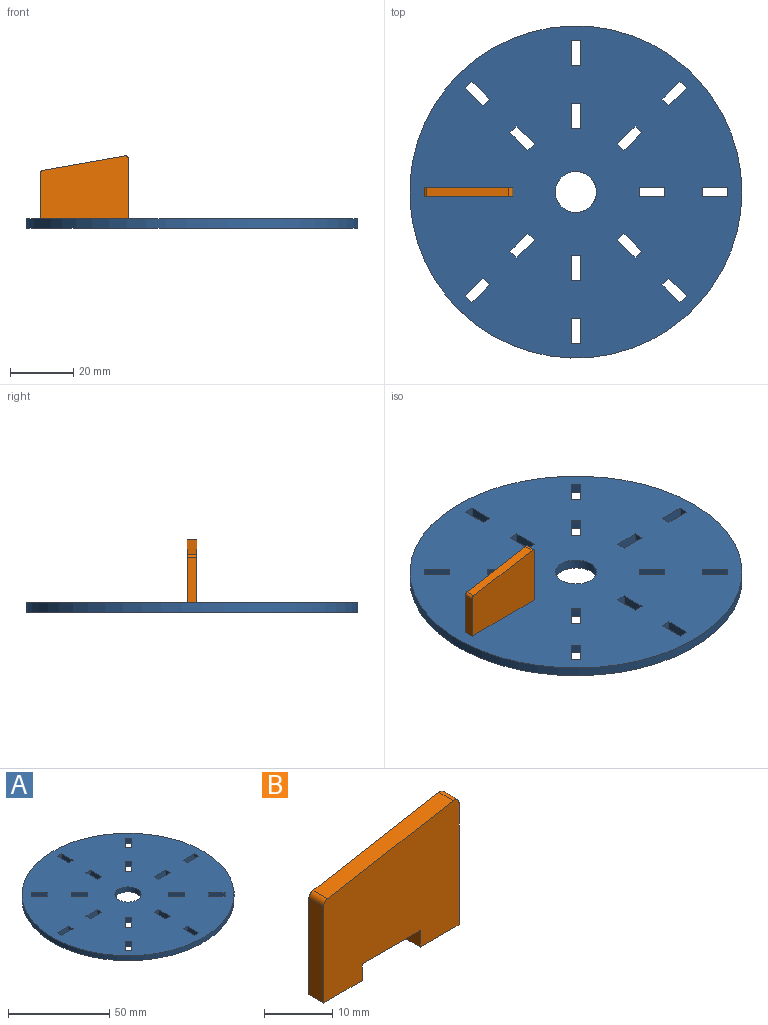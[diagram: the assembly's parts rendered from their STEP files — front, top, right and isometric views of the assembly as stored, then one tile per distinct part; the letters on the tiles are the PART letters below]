
ASSEMBLY  parts=2 mates=1
PART A: 68 faces, bbox 105x105x3 mm
  f0: plane 5.66x5.66mm, normal (-0.71,-0.71,0), area 24mm2, adj f1,f3,f56,f57
  f1: plane 3x2.13mm, normal (0.71,-0.71,0), area 9mm2, adj f0,f2,f56,f57
  f2: plane 5.66x5.66mm, normal (0.71,0.71,0), area 24mm2, adj f1,f3,f56,f57
  f3: plane 3x2.13mm, normal (-0.71,0.71,0), area 9mm2, adj f0,f2,f56,f57
  f4: plane 3x2.13mm, normal (-0.71,0.71,0), area 9mm2, adj f5,f7,f56,f57
  f5: plane 5.66x5.66mm, normal (0.71,0.71,0), area 24mm2, adj f4,f6,f56,f57
  f6: plane 3x2.13mm, normal (0.71,-0.71,0), area 9mm2, adj f5,f7,f56,f57
  f7: plane 5.66x5.66mm, normal (-0.71,-0.71,0), area 24mm2, adj f4,f6,f56,f57
  f8: plane 8.01x3mm, normal (-1,0,0), area 24mm2, adj f9,f11,f56,f57
  f9: plane 3.01x3mm, normal (0,-1,0), area 9mm2, adj f8,f10,f56,f57
  f10: plane 8.01x3mm, normal (1,0,0), area 24mm2, adj f9,f11,f56,f57
  f11: plane 3.01x3mm, normal (0,1,0), area 9mm2, adj f8,f10,f56,f57
  f12: plane 3.01x3mm, normal (0,1,0), area 9mm2, adj f13,f15,f56,f57
  f13: plane 8.01x3mm, normal (1,0,0), area 24mm2, adj f12,f14,f56,f57
  f14: plane 3.01x3mm, normal (0,-1,0), area 9mm2, adj f13,f15,f56,f57
  f15: plane 8.01x3mm, normal (-1,0,0), area 24mm2, adj f12,f14,f56,f57
  f16: plane 5.66x5.66mm, normal (-0.71,0.71,0), area 24mm2, adj f17,f19,f56,f57
  f17: plane 3x2.13mm, normal (-0.71,-0.71,0), area 9mm2, adj f16,f18,f56,f57
  f18: plane 5.66x5.66mm, normal (0.71,-0.71,0), area 24mm2, adj f17,f19,f56,f57
  f19: plane 3x2.13mm, normal (0.71,0.71,0), area 9mm2, adj f16,f18,f56,f57
  f20: plane 3x2.13mm, normal (0.71,0.71,0), area 9mm2, adj f21,f23,f56,f57
  f21: plane 5.66x5.66mm, normal (0.71,-0.71,0), area 24mm2, adj f20,f22,f56,f57
  f22: plane 3x2.13mm, normal (-0.71,-0.71,0), area 9mm2, adj f21,f23,f56,f57
  f23: plane 5.66x5.66mm, normal (-0.71,0.71,0), area 24mm2, adj f20,f22,f56,f57
  f24: plane 8.01x3mm, normal (0,1,0), area 24mm2, adj f25,f27,f56,f57
  f25: plane 3.01x3mm, normal (-1,0,0), area 9mm2, adj f24,f26,f56,f57
  f26: plane 8.01x3mm, normal (0,-1,0), area 24mm2, adj f25,f27,f56,f57
  f27: plane 3.01x3mm, normal (1,0,0), area 9mm2, adj f24,f26,f56,f57
  f28: plane 3.01x3mm, normal (1,0,0), area 9mm2, adj f29,f31,f56,f57
  f29: plane 8.01x3mm, normal (0,-1,0), area 24mm2, adj f28,f30,f56,f57
  f30: plane 3.01x3mm, normal (-1,0,0), area 9mm2, adj f29,f31,f56,f57
  f31: plane 8.01x3mm, normal (0,1,0), area 24mm2, adj f28,f30,f56,f57
  f32: plane 5.66x5.66mm, normal (0.71,0.71,0), area 24mm2, adj f33,f35,f56,f57
  f33: plane 3x2.13mm, normal (-0.71,0.71,0), area 9mm2, adj f32,f34,f56,f57
  f34: plane 5.66x5.66mm, normal (-0.71,-0.71,0), area 24mm2, adj f33,f35,f56,f57
  f35: plane 3x2.13mm, normal (0.71,-0.71,0), area 9mm2, adj f32,f34,f56,f57
  f36: plane 3x2.13mm, normal (0.71,-0.71,0), area 9mm2, adj f37,f39,f56,f57
  f37: plane 5.66x5.66mm, normal (-0.71,-0.71,0), area 24mm2, adj f36,f38,f56,f57
  f38: plane 3x2.13mm, normal (-0.71,0.71,0), area 9mm2, adj f37,f39,f56,f57
  f39: plane 5.66x5.66mm, normal (0.71,0.71,0), area 24mm2, adj f36,f38,f56,f57
  f40: plane 8.01x3mm, normal (1,0,0), area 24mm2, adj f41,f43,f56,f57
  f41: plane 3.01x3mm, normal (0,1,0), area 9mm2, adj f40,f42,f56,f57
  f42: plane 8.01x3mm, normal (-1,0,0), area 24mm2, adj f41,f43,f56,f57
  f43: plane 3.01x3mm, normal (0,-1,0), area 9mm2, adj f40,f42,f56,f57
  f44: plane 3.01x3mm, normal (0,-1,0), area 9mm2, adj f45,f47,f56,f57
  f45: plane 8.01x3mm, normal (-1,0,0), area 24mm2, adj f44,f46,f56,f57
  f46: plane 3.01x3mm, normal (0,1,0), area 9mm2, adj f45,f47,f56,f57
  f47: plane 8.01x3mm, normal (1,0,0), area 24mm2, adj f44,f46,f56,f57
  f48: plane 5.66x5.66mm, normal (0.71,-0.71,0), area 24mm2, adj f49,f51,f56,f57
  f49: plane 3x2.13mm, normal (0.71,0.71,0), area 9mm2, adj f48,f50,f56,f57
  f50: plane 5.66x5.66mm, normal (-0.71,0.71,0), area 24mm2, adj f49,f51,f56,f57
  f51: plane 3x2.13mm, normal (-0.71,-0.71,0), area 9mm2, adj f48,f50,f56,f57
  f52: plane 3x2.13mm, normal (-0.71,-0.71,0), area 9mm2, adj f53,f55,f56,f57
  f53: plane 5.66x5.66mm, normal (-0.71,0.71,0), area 24mm2, adj f52,f54,f56,f57
  f54: plane 3x2.13mm, normal (0.71,0.71,0), area 9mm2, adj f53,f55,f56,f57
  f55: plane 5.66x5.66mm, normal (0.71,-0.71,0), area 24mm2, adj f52,f54,f56,f57
  f56: plane 105x105mm, normal (0,0,1), area 8140.3mm2, adj f0,f1,f2,f3,f4,f5,f6,f7
  f57: plane 105x105mm, normal (0,0,-1), area 8140.3mm2, adj f0,f1,f2,f3,f4,f5,f6,f7
  f58: cylinder r=52.5mm len=105mm, axis (0,0,-1), area 989.6mm2, adj f56,f57
  f59: plane 8.01x3mm, normal (0,-1,0), area 24mm2, adj f56,f57,f60,f62
  f60: plane 3.01x3mm, normal (1,0,0), area 9mm2, adj f56,f57,f59,f61
  f61: plane 8.01x3mm, normal (0,1,0), area 24mm2, adj f56,f57,f60,f62
  f62: plane 3.01x3mm, normal (-1,0,0), area 9mm2, adj f56,f57,f59,f61
  f63: plane 8.01x3mm, normal (0,-1,0), area 24mm2, adj f56,f57,f64,f66
  f64: plane 3.01x3mm, normal (1,0,0), area 9mm2, adj f56,f57,f63,f65
  f65: plane 8.01x3mm, normal (0,1,0), area 24mm2, adj f56,f57,f64,f66
  f66: plane 3.01x3mm, normal (-1,0,0), area 9mm2, adj f56,f57,f63,f65
  f67: cylinder r=6.51mm len=13.01mm, axis (0,0,-1), area 122.6mm2, adj f56,f57
PART B: 12 faces, bbox 28x3x22.8 mm
  f0: plane 8x3mm, normal (0,0,-1), area 24mm2, adj f1,f2,f5,f8
  f1: plane 28x22.81mm, normal (0,-1,0), area 538.4mm2, adj f0,f3,f4,f5,f6,f7,f8,f9
  f2: plane 28x22.81mm, normal (0,1,0), area 538.4mm2, adj f0,f3,f4,f5,f6,f7,f8,f9
  f3: plane 17.22x3mm, normal (-1,0,0), area 51.7mm2, adj f1,f2,f4,f11
  f4: plane 8x3mm, normal (0,0,-1), area 24mm2, adj f1,f2,f3,f7
  f5: plane 21.81x3mm, normal (1,0,0), area 65.4mm2, adj f0,f1,f2,f10
  f6: plane 26x4.58mm, normal (-0.17,0,0.98), area 79.2mm2, adj f1,f2,f10,f11
  f7: plane 3x3mm, normal (1,0,0), area 9mm2, adj f1,f2,f4,f9
  f8: plane 3x3mm, normal (-1,0,0), area 9mm2, adj f0,f1,f2,f9
  f9: plane 12x3mm, normal (0,0,-1), area 36mm2, adj f1,f2,f7,f8
  f10: cylinder r=1mm len=3mm, axis (0,1,0), area 5.2mm2, adj f1,f2,f5,f6
  f11: cylinder r=1mm len=3mm, axis (0,1,0), area 4.2mm2, adj f1,f2,f3,f6
PLACE A at identity fixed
PLACE B t=(-19.99,0,-1.5)mm
MATE fastened B.f4 <-> A.f57  axis (0,0,-1) through (-43.99,0,-1.5)mm
